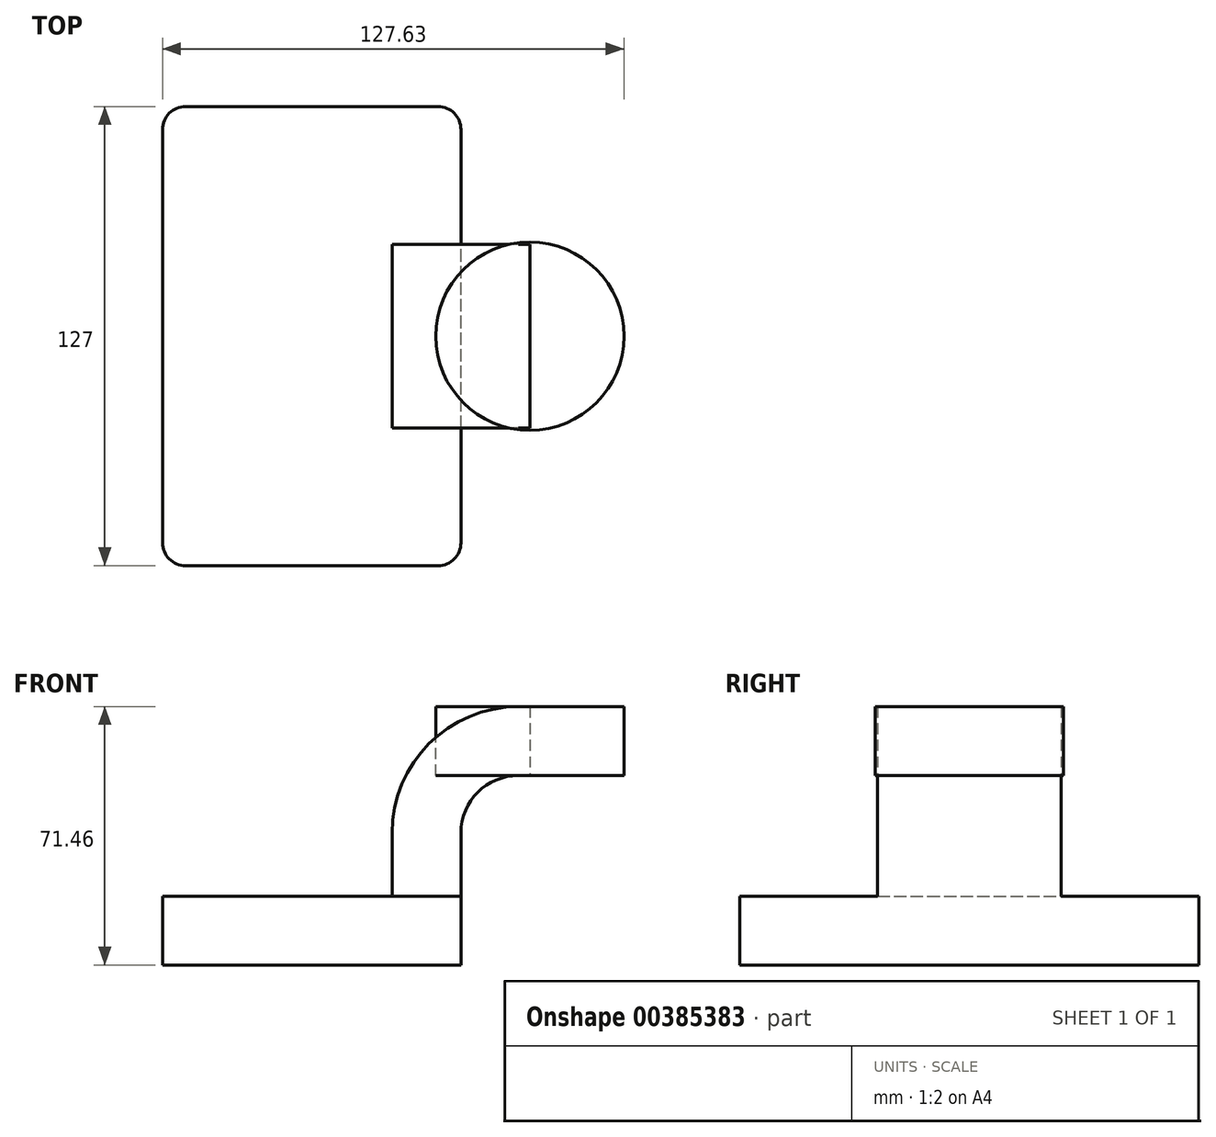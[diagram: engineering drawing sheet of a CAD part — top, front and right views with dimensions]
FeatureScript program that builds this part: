
annotation { "Feature Type Name" : "Feature", "Feature Type Description" : "" }
export const myFeature = defineFeature(function(context is Context, id is Id, definition is map)
    precondition{}
    {
        {
            var Q0;
            Q0=qCreatedBy(makeId("Front.planeOp"),FACE);
            var sketch = newSketch(context, id + "F0", { "sketchPlane" : qUnion([Q0])});
            skLineSegment(sketch, "E0.bottom", {"start": v(-41.28, 9.52) * mm, "end": v(41.27, 9.53) * mm});
            skLineSegment(sketch, "E0.top", {"start": v(-41.28, -9.53) * mm, "end": v(41.28, -9.53) * mm});
            skLineSegment(sketch, "E0.left", {"start": v(-41.28, 9.52) * mm, "end": v(-41.28, -9.53) * mm});
            skLineSegment(sketch, "E0.right", {"start": v(41.27, 9.53) * mm, "end": v(41.28, -9.52) * mm});
            skPoint(sketch, "E0.middle", {"position": v(0, 0) * mm});
            skLineSegment(sketch, "E1.bottom", {"start": v(60.32, 66.68) * mm, "end": v(111.12, 66.68) * mm});
            skLineSegment(sketch, "E1.top", {"start": v(60.32, 38.1) * mm, "end": v(111.12, 38.1) * mm});
            skLineSegment(sketch, "E1.left", {"start": v(60.32, 66.68) * mm, "end": v(60.32, 38.1) * mm});
            skLineSegment(sketch, "E1.right", {"start": v(111.12, 66.68) * mm, "end": v(111.12, 38.1) * mm});
            skPoint(sketch, "E1.middle", {"position": v(85.72, 52.39) * mm});
            skLineSegment(sketch, "E2", {"start": v(41.27, 9.53) * mm, "end": v(41.27, 27) * mm});
            skArc(sketch, "E3", {"start": v(41.27, 27) * mm, "mid": v(45.92, 38.23) * mm, "end": v(57.15, 42.88) * mm});
            skLineSegment(sketch, "E4", {"start": v(57.15, 42.88) * mm, "end": v(86.36, 42.88) * mm});
            skLineSegment(sketch, "E5.0", {"start": v(57.15, 61.93) * mm, "end": v(86.36, 61.93) * mm});
            skArc(sketch, "E5.1", {"start": v(22.22, 27) * mm, "mid": v(32.45, 51.7) * mm, "end": v(57.15, 61.93) * mm});
            skLineSegment(sketch, "E5.2", {"start": v(22.22, 9.53) * mm, "end": v(22.22, 27) * mm});
            skLineSegment(sketch, "E6", {"start": v(86.36, 38.1) * mm, "end": v(86.36, 66.68) * mm});
            skFitSpline(sketch, "E7", {"points": [v(-41.28, 9.52) * mm, v(57.15, 61.93) * mm], "startDerivative": vector(22.3, 88.05) * mm, "endDerivative": vector(198.9, -2.2) * mm});
            skSolve(sketch);
        }
        {
            var Q0;
            Q0=makeQuery(id+"F0.imprint","IMPRINT",FACE,{"disambiguationData":[TD([[makeQuery(id+"F0.imprint","IMPRINT",EDGE,{"derivedFrom":sQuery(id+"F0.wireOp",EDGE,"E0.top")}),1.0]])]});
            extrude(context, id + "F1", {"entities" : qUnion([Q0]), "endBound" : BoundingType.SYMMETRIC, "depth" : 127 * mm});
        }
        {
            var Q0;
            {var subQ1=sQuery(id+"F0.wireOp",EDGE,"E2");Q0=makeQuery(id+"F0.imprint","IMPRINT",FACE,{"disambiguationData":[TD([[makeQuery(id+"F0.imprint","IMPRINT",EDGE,{"derivedFrom":subQ1}),1.0]])]});}
            extrude(context, id + "F2", {"entities" : qUnion([Q0]), "operationType" : NewBodyOperationType.ADD, "endBound" : BoundingType.SYMMETRIC, "depth" : 50.8 * mm});
        }
        {
            var Q0;
            Q0=makeQuery(id+"F0.imprint","IMPRINT",FACE,{"disambiguationData":[TD([[makeQuery(id+"F0.imprint","IMPRINT",EDGE,{"derivedFrom":sQuery(id+"F0.wireOp",EDGE,"E5.1")}),1.0]])]});
            extrude(context, id + "F3", {"entities" : qUnion([Q0]), "operationType" : NewBodyOperationType.ADD, "endBound" : BoundingType.SYMMETRIC, "depth" : 15.88 * mm});
        }
        {
            var Q0;
            {var subQ0=sQuery(id+"F0.wireOp",EDGE,"E5.0");var subQ1=sQuery(id+"F0.wireOp",EDGE,"E1.left");var subQ2=makeQuery(id+"F0.imprint","INTERSECT",VERTEX,{"derivedFrom":[subQ1,subQ0]});Q0=makeQuery(id+"F0.imprint","IMPRINT",FACE,{"disambiguationData":[TD([[makeQuery(id+"F0.imprint","IMPRINT",EDGE,{"disambiguationData":[TD([[subQ2,-1.0]])],"derivedFrom":subQ1}),1.0]])]});}
            var Q1;
            Q1=sQuery(id+"F0.wireOp",EDGE,"E1.left");
            revolve(context, id + "F4", {"entities" : qUnion([Q0]), "axis" : qUnion([Q1]), "revolveType" : RevolveType.FULL});
        }
        {
            var Q0;
            Q0=makeQuery(id+"F1.opExtrude","CAP_EDGE",EDGE,{"disambiguationData":[OSD([sQuery(id+"F0.wireOp",EDGE,"E0.left")])],"isStart":false});
            var Q1;
            Q1=makeQuery(id+"F1.opExtrude","CAP_EDGE",EDGE,{"disambiguationData":[OSD([sQuery(id+"F0.wireOp",EDGE,"E0.right")])],"isStart":false});
            var Q2;
            Q2=makeQuery(id+"F1.opExtrude","CAP_EDGE",EDGE,{"disambiguationData":[OSD([sQuery(id+"F0.wireOp",EDGE,"E0.right")])],"isStart":true});
            var Q3;
            Q3=makeQuery(id+"F1.opExtrude","CAP_EDGE",EDGE,{"disambiguationData":[OSD([sQuery(id+"F0.wireOp",EDGE,"E0.left")])],"isStart":true});
            fillet(context, id + "F5", {"entities" : qUnion([Q0, Q1, Q2, Q3]), "radius" : 6.35 * mm, "tangentPropagation" : true, "allowEdgeOverflow" : false});
        }
    });
